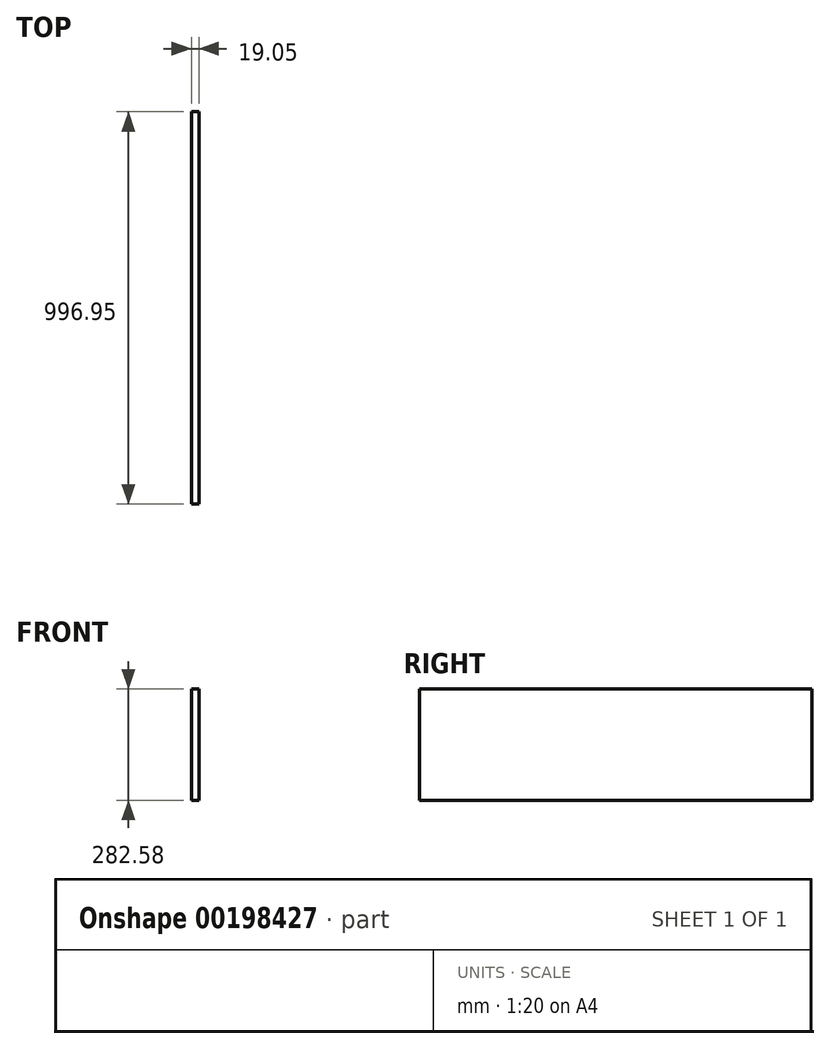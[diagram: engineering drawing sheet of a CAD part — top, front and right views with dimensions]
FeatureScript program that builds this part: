
annotation { "Feature Type Name" : "Feature", "Feature Type Description" : "" }
export const myFeature = defineFeature(function(context is Context, id is Id, definition is map)
    precondition{}
    {
        {
            var Q0;
            Q0=qCreatedBy(makeId("Right.planeOp"),FACE);
            var sketch = newSketch(context, id + "F0", { "sketchPlane" : qUnion([Q0])});
            skLineSegment(sketch, "E0.bottom", {"start": v(-547.46, 141.29) * mm, "end": v(449.5, 141.29) * mm});
            skLineSegment(sketch, "E0.top", {"start": v(-547.46, -141.29) * mm, "end": v(449.5, -141.29) * mm});
            skLineSegment(sketch, "E0.left", {"start": v(-547.46, 141.29) * mm, "end": v(-547.46, -141.29) * mm});
            skLineSegment(sketch, "E0.right", {"start": v(449.5, 141.29) * mm, "end": v(449.5, -141.29) * mm});
            skPoint(sketch, "E0.middle", {"position": v(-48.98, 0) * mm});
            skSolve(sketch);
        }
        {
            var Q0;
            Q0=makeQuery(id+"F0.imprint","IMPRINT",FACE,{"disambiguationData":[TD([[makeQuery(id+"F0.imprint","IMPRINT",EDGE,{"derivedFrom":sQuery(id+"F0.wireOp",EDGE,"E0.bottom")}),-1.0]])]});
            extrude(context, id + "F1", {"entities" : qUnion([Q0]), "depth" : 19.05 * mm});
        }
    });
